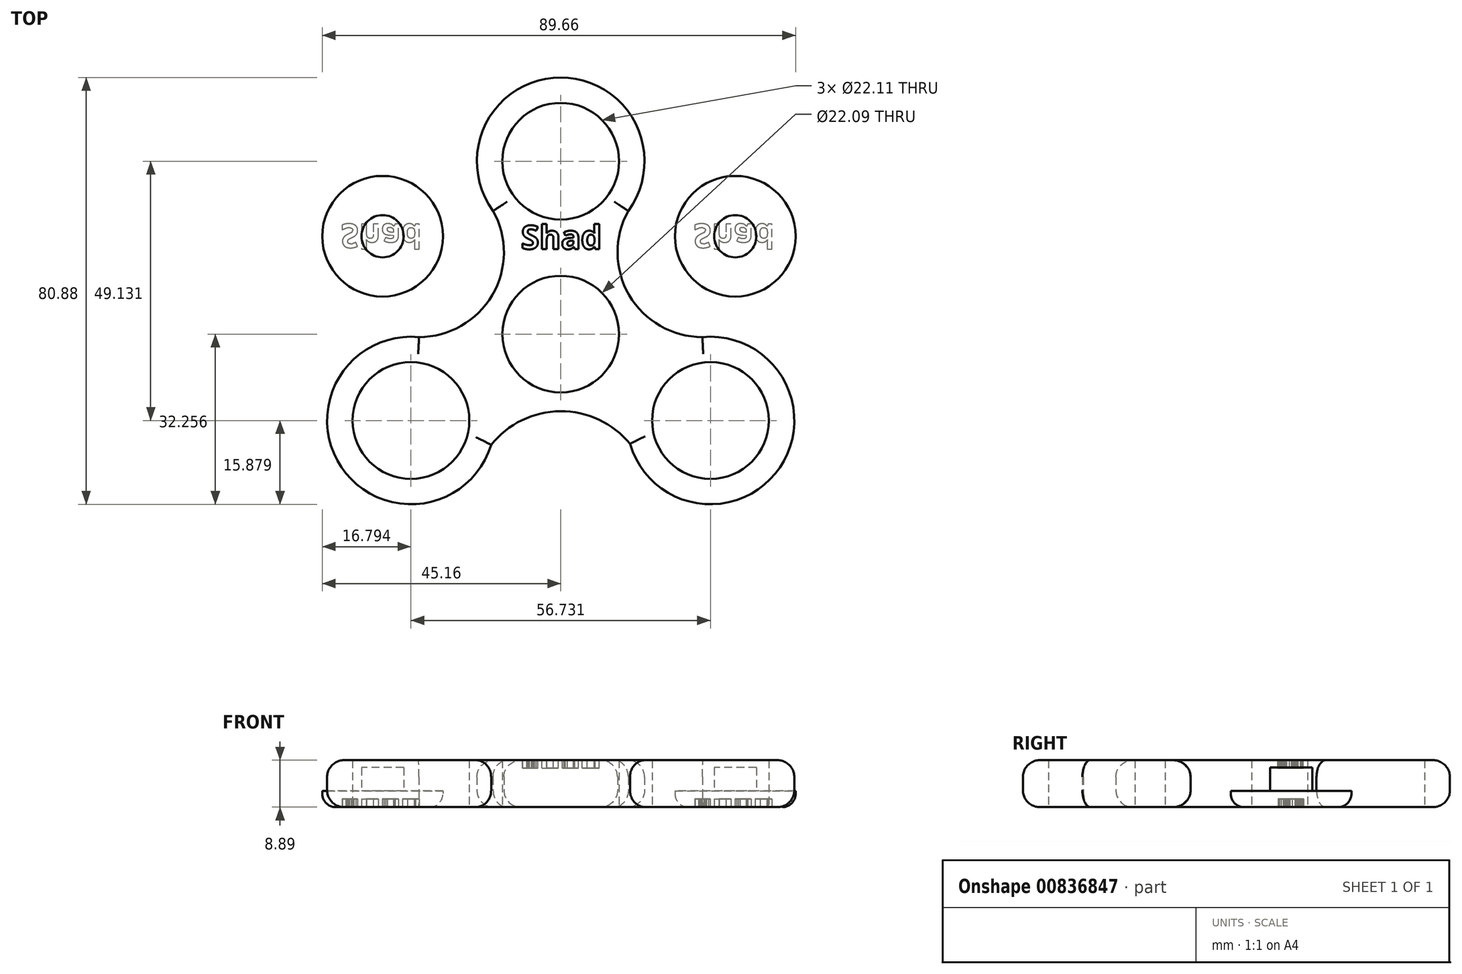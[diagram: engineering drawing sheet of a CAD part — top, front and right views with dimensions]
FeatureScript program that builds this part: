
annotation { "Feature Type Name" : "Feature", "Feature Type Description" : "" }
export const myFeature = defineFeature(function(context is Context, id is Id, definition is map)
    precondition{}
    {
        {
            var Q0;
            Q0=qCreatedBy(makeId("Top.planeOp"),FACE);
            var sketch = newSketch(context, id + "F0", { "sketchPlane" : qUnion([Q0])});
            skCircle(sketch, "E0", {"center": v(0, 61.7) * mm, "radius": 11.06 * mm});
            skCircle(sketch, "E1.1.0", {"center": v(-28.37, 12.58) * mm, "radius": 11.06 * mm});
            skCircle(sketch, "E1.2.0", {"center": v(28.37, 12.58) * mm, "radius": 11.06 * mm});
            skPoint(sketch, "E1.center", {"position": v(0, 28.96) * mm});
            skCircle(sketch, "E2", {"center": v(0, 28.96) * mm, "radius": 11.04 * mm});
            skArc(sketch, "E3", {"start": v(12.8, 52.32) * mm, "mid": v(0, 77.58) * mm, "end": v(-12.8, 52.32) * mm});
            skArc(sketch, "E4", {"start": v(-26.83, 28.38) * mm, "mid": v(-41.56, 3.75) * mm, "end": v(-13.17, 7.97) * mm});
            skArc(sketch, "E5", {"start": v(13.12, 8.14) * mm, "mid": v(41.51, 3.68) * mm, "end": v(26.83, 28.38) * mm});
            skArc(sketch, "E6", {"start": v(-26.83, 28.38) * mm, "mid": v(-12.5, 37.21) * mm, "end": v(-13.87, 54) * mm});
            skArc(sketch, "E7.MirrorCS", {"start": v(26.83, 28.38) * mm, "mid": v(12.5, 37.21) * mm, "end": v(13.87, 54) * mm});
            skArc(sketch, "E8", {"start": v(16.22, 2.35) * mm, "mid": v(0.13, 14.33) * mm, "end": v(-16.08, 2.52) * mm});
            skSolve(sketch);
        }
        {
            var Q0;
            Q0=qSketchRegion(id+"F0",true);
            extrude(context, id + "F1", {"entities" : qUnion([Q0]), "depth" : 8.9 * mm, "offsetDistance" : 25.4 * mm});
        }
        {
            var Q0;
            Q0=makeQuery(id+"F1.opExtrude","CAP_EDGE",EDGE,{"disambiguationData":[OSD([sQuery(id+"F0.wireOp",EDGE,"E8")])],"isStart":false});
            var Q1;
            Q1=makeQuery(id+"F1.opExtrude","CAP_EDGE",EDGE,{"disambiguationData":[OSD([sQuery(id+"F0.wireOp",EDGE,"E4")])],"isStart":false});
            var Q2;
            Q2=makeQuery(id+"F1.opExtrude","CAP_EDGE",EDGE,{"disambiguationData":[OSD([sQuery(id+"F0.wireOp",EDGE,"E6")])],"isStart":false});
            var Q3;
            Q3=makeQuery(id+"F1.opExtrude","CAP_EDGE",EDGE,{"disambiguationData":[OSD([sQuery(id+"F0.wireOp",EDGE,"E3")])],"isStart":false});
            var Q4;
            Q4=makeQuery(id+"F1.opExtrude","CAP_EDGE",EDGE,{"disambiguationData":[OSD([sQuery(id+"F0.wireOp",EDGE,"E5")])],"isStart":false});
            var Q5;
            Q5=makeQuery(id+"F1.opExtrude","CAP_EDGE",EDGE,{"disambiguationData":[OSD([sQuery(id+"F0.wireOp",EDGE,"E7.MirrorCS")])],"isStart":false});
            var Q6;
            Q6=makeQuery(id+"F1.opExtrude","CAP_EDGE",EDGE,{"disambiguationData":[OSD([sQuery(id+"F0.wireOp",EDGE,"E7.MirrorCS")])],"isStart":true});
            var Q7;
            Q7=makeQuery(id+"F1.opExtrude","CAP_EDGE",EDGE,{"disambiguationData":[OSD([sQuery(id+"F0.wireOp",EDGE,"E3")])],"isStart":true});
            var Q8;
            Q8=makeQuery(id+"F1.opExtrude","CAP_EDGE",EDGE,{"disambiguationData":[OSD([sQuery(id+"F0.wireOp",EDGE,"E5")])],"isStart":true});
            var Q9;
            Q9=makeQuery(id+"F1.opExtrude","CAP_EDGE",EDGE,{"disambiguationData":[OSD([sQuery(id+"F0.wireOp",EDGE,"E8")])],"isStart":true});
            var Q10;
            Q10=makeQuery(id+"F1.opExtrude","CAP_EDGE",EDGE,{"disambiguationData":[OSD([sQuery(id+"F0.wireOp",EDGE,"E4")])],"isStart":true});
            var Q11;
            Q11=makeQuery(id+"F1.opExtrude","CAP_EDGE",EDGE,{"disambiguationData":[OSD([sQuery(id+"F0.wireOp",EDGE,"E6")])],"isStart":true});
            fillet(context, id + "F2", {"entities" : qUnion([Q0, Q1, Q2, Q3, Q4, Q5, Q6, Q7, Q8, Q9, Q10, Q11]), "radius" : 3.17 * mm, "tangentPropagation" : true, "allowEdgeOverflow" : false});
        }
        {
            var Q0;
            Q0=qCreatedBy(makeId("Top.planeOp"),FACE);
            var sketch = newSketch(context, id + "F3", { "sketchPlane" : qUnion([Q0])});
            skCircle(sketch, "E9", {"center": v(33.07, 47.5) * mm, "radius": 11.43 * mm});
            skSolve(sketch);
        }
        {
            var Q0;
            Q0=makeQuery(id+"F3.imprint","IMPRINT",FACE,{"disambiguationData":[TD([[makeQuery(id+"F3.imprint","IMPRINT",EDGE,{"derivedFrom":sQuery(id+"F3.wireOp",EDGE,"E9")}),1.0]])]});
            extrude(context, id + "F4", {"entities" : qUnion([Q0]), "depth" : 3.05 * mm, "offsetDistance" : 25.4 * mm});
        }
        {
            var Q0;
            Q0=makeQuery(id+"F4.opExtrude","CAP_FACE",FACE,{"disambiguationData":[OSD([sQuery(id+"F3.wireOp",EDGE,"E9")])],"isStart":false});
            var sketch = newSketch(context, id + "F5", { "sketchPlane" : qUnion([Q0])});
            skCircle(sketch, "E10", {"center": v(33.07, 47.5) * mm, "radius": 4 * mm});
            skSolve(sketch);
        }
        {
            var Q0;
            Q0=makeQuery(id+"F5.imprint","IMPRINT",FACE,{"disambiguationData":[TD([[makeQuery(id+"F5.imprint","IMPRINT",EDGE,{"derivedFrom":sQuery(id+"F5.wireOp",EDGE,"E10")}),1.0]])]});
            extrude(context, id + "F6", {"entities" : qUnion([Q0]), "operationType" : NewBodyOperationType.ADD, "depth" : 4.44 * mm, "offsetDistance" : 25.4 * mm});
        }
        {
            var Q0;
            Q0=makeQuery(id+"F4.opExtrude","CAP_EDGE",EDGE,{"disambiguationData":[OSD([sQuery(id+"F3.wireOp",EDGE,"E9")])],"isStart":true});
            fillet(context, id + "F7", {"entities" : qUnion([Q0]), "radius" : 2.54 * mm, "tangentPropagation" : true, "allowEdgeOverflow" : false});
        }
        {
            var Q0;
            Q0=makeQuery(id+"F4.opExtrude","CAP_FACE",FACE,{"disambiguationData":[OSD([sQuery(id+"F3.wireOp",EDGE,"E9")])],"isStart":true});
            var sketch = newSketch(context, id + "F8", { "sketchPlane" : qUnion([Q0])});
            skText(sketch, "E11", { "text": "Shad", "fontName": "OpenSans-Bold.ttf"});
            const initialGuessF8  = {"E11": [0.02513, -0.04983, 1, 0, 0.00453]};
            skSetInitialGuess(sketch, initialGuessF8);
            skSolve(sketch);
        }
        {
            var Q0;
            Q0=qSketchRegion(id+"F8",true);
            extrude(context, id + "F9", {"entities" : qUnion([Q0]), "operationType" : NewBodyOperationType.REMOVE, "oppositeDirection" : true, "depth" : 1.52 * mm, "offsetDistance" : 25.4 * mm});
        }
        {
            var Q0;
            Q0=makeQuery(id+"F4.opExtrude","SWEPT_BODY",BODY,{"disambiguationData":[OSD([sQuery(id+"F3.wireOp",EDGE,"E9")])]});
            transform(context, id + "F10", {"entities" : qUnion([Q0]), "transformType" : TransformType.TRANSLATION_3D, "dx" : -66.8 * mm, "dy" : 0 * mm, "dz" : 0 * mm, "makeCopy" : true});
        }
        {
            var Q0;
            Q0=makeQuery(id+"F1.opExtrude","CAP_FACE",FACE,{"disambiguationData":[OSD([sQuery(id+"F0.wireOp",EDGE,"E0"),sQuery(id+"F0.wireOp",EDGE,"E1.1.0"),sQuery(id+"F0.wireOp",EDGE,"E1.2.0"),sQuery(id+"F0.wireOp",EDGE,"E2"),sQuery(id+"F0.wireOp",EDGE,"E3"),sQuery(id+"F0.wireOp",EDGE,"E4"),sQuery(id+"F0.wireOp",EDGE,"E5"),sQuery(id+"F0.wireOp",EDGE,"E6"),sQuery(id+"F0.wireOp",EDGE,"E7.MirrorCS"),sQuery(id+"F0.wireOp",EDGE,"E8")])],"isStart":false});
            var sketch = newSketch(context, id + "F11", { "sketchPlane" : qUnion([Q0])});
            skText(sketch, "E12", { "text": "Shad", "fontName": "OpenSans-Bold.ttf"});
            const initialGuessF11  = {"E12": [-0.00752, 0.04507, 1, 0, 0.0045]};
            skSetInitialGuess(sketch, initialGuessF11);
            skSolve(sketch);
        }
        {
            var Q0;
            Q0=qSketchRegion(id+"F11",true);
            extrude(context, id + "F12", {"entities" : qUnion([Q0]), "operationType" : NewBodyOperationType.REMOVE, "oppositeDirection" : true, "depth" : 1.52 * mm, "offsetDistance" : 25.4 * mm});
        }
    });
